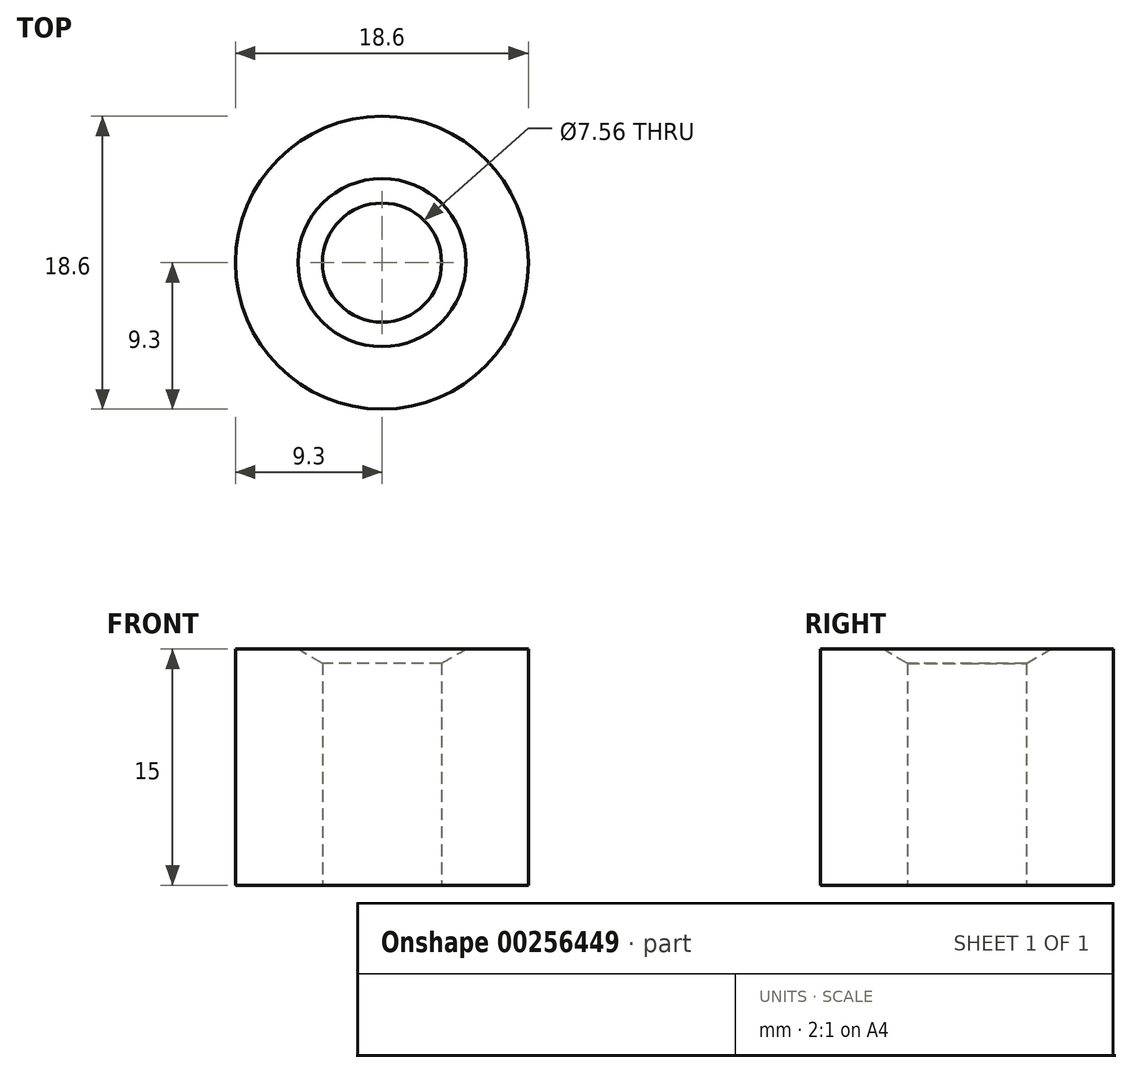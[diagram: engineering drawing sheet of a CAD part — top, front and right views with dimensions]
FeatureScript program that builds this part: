
annotation { "Feature Type Name" : "Feature", "Feature Type Description" : "" }
export const myFeature = defineFeature(function(context is Context, id is Id, definition is map)
    precondition{}
    {
        {
            var Q0;
            Q0=qCreatedBy(makeId("Top.planeOp"),FACE);
            var sketch = newSketch(context, id + "F0", { "sketchPlane" : qUnion([Q0])});
            skCircle(sketch, "E0", {"center": v(0, 0) * mm, "radius": 3.1 * mm});
            skCircle(sketch, "E1", {"center": v(0, 0) * mm, "radius": 1.26 * mm});
            skSolve(sketch);
        }
        {
            var Q0;
            Q0=makeQuery(id+"F0.imprint","IMPRINT",FACE,{"disambiguationData":[TD([[makeQuery(id+"F0.imprint","IMPRINT",EDGE,{"derivedFrom":sQuery(id+"F0.wireOp",EDGE,"E0")}),1.0]])]});
            extrude(context, id + "F1", {"entities" : qUnion([Q0]), "depth" : 5 * mm});
        }
        {
            var Q0;
            Q0=makeQuery(id+"F1.opExtrude","CAP_EDGE",EDGE,{"disambiguationData":[OSD([sQuery(id+"F0.wireOp",EDGE,"E1")])],"isStart":false});
            chamfer(context, id + "F2", {"entities" : qUnion([Q0]), "chamferType" : ChamferType.OFFSET_ANGLE, "width" : 0.3 * mm, "oppositeDirection" : true, "angle" : 60 * degree, "tangentPropagation" : true});
        }
        {
            var Q0;
            Q0=makeQuery(id+"F1.opExtrude","SWEPT_BODY",BODY,{"disambiguationData":[OSD([sQuery(id+"F0.wireOp",EDGE,"E0"),sQuery(id+"F0.wireOp",EDGE,"E1")])]});
            var Q1;
            Q1=qCreatedBy(makeId("Origin.pointOp"),VERTEX);
            transform(context, id + "F3", {"entities" : qUnion([Q0]), "transformType" : TransformType.SCALE_UNIFORMLY, "scale" : 3, "makeCopy" : false, "scalePoint" : qUnion([Q1])});
        }
    });
